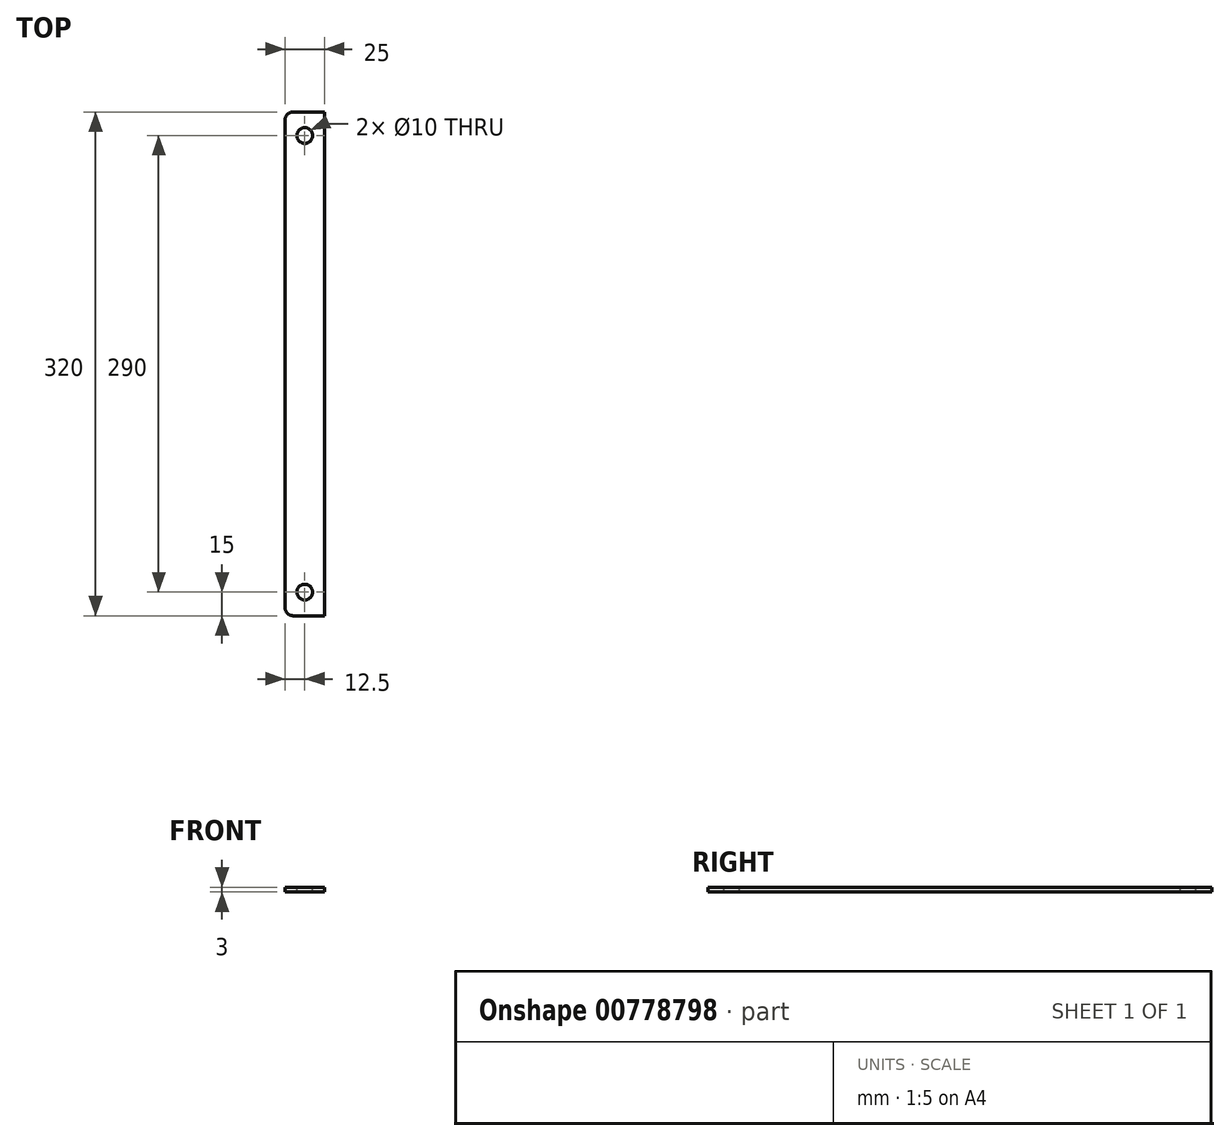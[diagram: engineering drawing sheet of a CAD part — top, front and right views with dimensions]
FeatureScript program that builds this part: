
annotation { "Feature Type Name" : "Feature", "Feature Type Description" : "" }
export const myFeature = defineFeature(function(context is Context, id is Id, definition is map)
    precondition{}
    {
        {
            var Q0;
            Q0=qCreatedBy(makeId("Top.planeOp"),FACE);
            var sketch = newSketch(context, id + "F0", { "sketchPlane" : qUnion([Q0])});
            skLineSegment(sketch, "E0.bottom", {"start": v(5, 0) * mm, "end": v(25, 0) * mm});
            skLineSegment(sketch, "E0.top", {"start": v(5, 320) * mm, "end": v(25, 320) * mm});
            skLineSegment(sketch, "E0.left", {"start": v(0, 5) * mm, "end": v(0, 315) * mm});
            skLineSegment(sketch, "E0.right", {"start": v(25, 0) * mm, "end": v(25, 320) * mm});
            skPoint(sketch, "E1.visualSharp", {"position": v(0, 320) * mm});
            skArc(sketch, "E1.filletArc", {"start": v(5, 320) * mm, "mid": v(1.46, 318.54) * mm, "end": v(0, 315) * mm});
            skPoint(sketch, "E2.visualSharp", {"position": v(0, 0) * mm});
            skArc(sketch, "E2.filletArc", {"start": v(0, 5) * mm, "mid": v(1.46, 1.46) * mm, "end": v(5, 0) * mm});
            skSolve(sketch);
        }
        {
            var Q0;
            Q0=qSketchRegion(id+"F0",true);
            extrude(context, id + "F1", {"entities" : qUnion([Q0]), "depth" : 3 * mm, "offsetDistance" : 25 * mm});
        }
        {
            var Q0;
            Q0=makeQuery(id+"F1.opExtrude","CAP_FACE",FACE,{"disambiguationData":[OSD([sQuery(id+"F0.wireOp",EDGE,"E0.bottom"),sQuery(id+"F0.wireOp",EDGE,"E0.top"),sQuery(id+"F0.wireOp",EDGE,"E0.left"),sQuery(id+"F0.wireOp",EDGE,"E0.right"),sQuery(id+"F0.wireOp",EDGE,"E1.filletArc"),sQuery(id+"F0.wireOp",EDGE,"E2.filletArc")])],"isStart":false});
            var sketch = newSketch(context, id + "F2", { "sketchPlane" : qUnion([Q0])});
            skCircle(sketch, "E3", {"center": v(12.5, 305) * mm, "radius": 5 * mm});
            skLineSegment(sketch, "E4", {"start": v(25, 160) * mm, "end": v(-52.83, 160) * mm, "construction": true});
            skCircle(sketch, "E5.MirrorC", {"center": v(12.5, 15) * mm, "radius": 5 * mm});
            skSolve(sketch);
        }
        {
            var Q0;
            Q0=qSketchRegion(id+"F2",true);
            extrude(context, id + "F3", {"entities" : qUnion([Q0]), "operationType" : NewBodyOperationType.REMOVE, "endBound" : BoundingType.UP_TO_NEXT, "oppositeDirection" : true, "depth" : 25 * mm, "offsetDistance" : 25 * mm});
        }
    });
